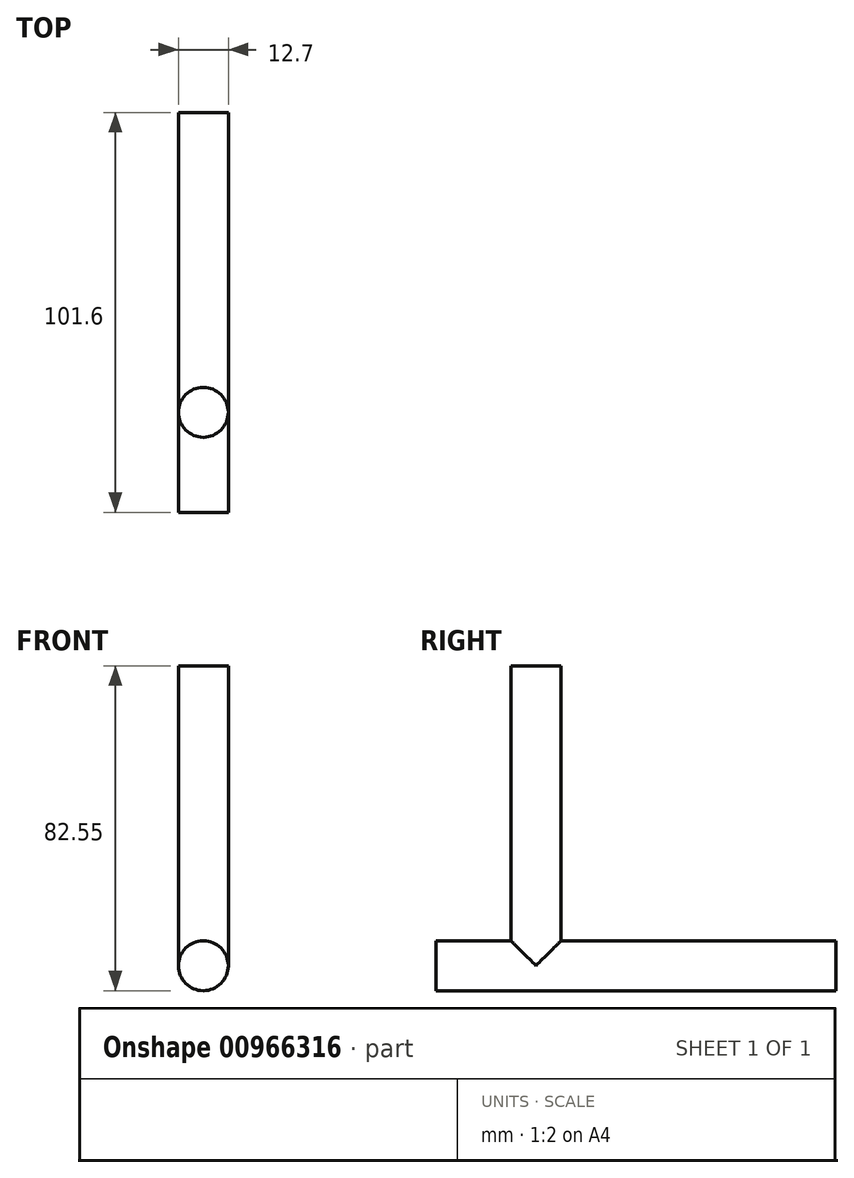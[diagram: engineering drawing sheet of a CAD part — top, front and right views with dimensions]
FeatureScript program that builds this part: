
annotation { "Feature Type Name" : "Feature", "Feature Type Description" : "" }
export const myFeature = defineFeature(function(context is Context, id is Id, definition is map)
    precondition{}
    {
        {
            var Q0;
            Q0=qCreatedBy(makeId("Top.planeOp"),FACE);
            var sketch = newSketch(context, id + "F0", { "sketchPlane" : qUnion([Q0])});
            skCircle(sketch, "E0", {"center": v(0, 0) * mm, "radius": 6.35 * mm});
            skSolve(sketch);
        }
        {
            var Q0;
            Q0 = qSketchRegion(id + "F0", true);
            extrude(context, id + "F1", {"entities" : qUnion([Q0]), "depth" : 76.2 * mm, "offsetDistance" : 25.4 * mm});
        }
        {
            var Q0;
            Q0=qCreatedBy(makeId("Front.planeOp"),FACE);
            var sketch = newSketch(context, id + "F2", { "sketchPlane" : qUnion([Q0])});
            skCircle(sketch, "E1", {"center": v(0, 0) * mm, "radius": 6.35 * mm});
            skSolve(sketch);
        }
        {
            var Q0;
            Q0 = qSketchRegion(id + "F2", true);
            extrude(context, id + "F3", {"entities" : qUnion([Q0]), "operationType" : NewBodyOperationType.ADD, "oppositeDirection" : true, "depth" : 76.2 * mm, "offsetDistance" : 25.4 * mm, "hasSecondDirection" : true, "secondDirectionOppositeDirection" : false, "secondDirectionDepth" : 25.4 * mm});
        }
    });
